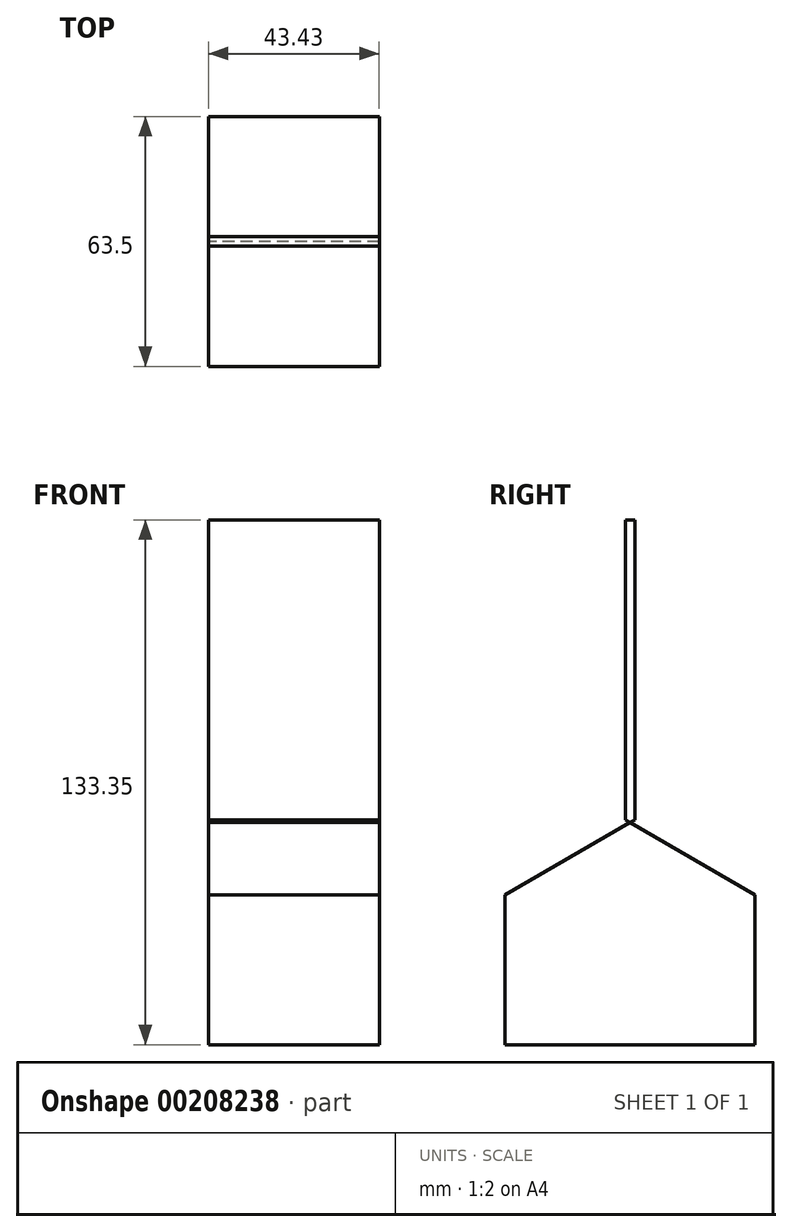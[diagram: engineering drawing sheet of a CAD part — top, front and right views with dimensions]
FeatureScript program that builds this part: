
annotation { "Feature Type Name" : "Feature", "Feature Type Description" : "" }
export const myFeature = defineFeature(function(context is Context, id is Id, definition is map)
    precondition{}
    {
        {
            var Q0;
            Q0=qCreatedBy(makeId("Right.planeOp"),FACE);
            var sketch = newSketch(context, id + "F0", { "sketchPlane" : qUnion([Q0])});
            skLineSegment(sketch, "E0.bottom", {"start": v(-31.75, -65.47) * mm, "end": v(31.75, -65.47) * mm});
            skLineSegment(sketch, "E0.left", {"start": v(-31.75, -65.47) * mm, "end": v(-31.75, -27.37) * mm});
            skLineSegment(sketch, "E0.right", {"start": v(31.75, -65.47) * mm, "end": v(31.75, -27.37) * mm});
            skPoint(sketch, "E0.middle", {"position": v(0, -46.42) * mm});
            skLineSegment(sketch, "E1", {"start": v(31.75, -27.37) * mm, "end": v(-1.25, -8.32) * mm});
            skLineSegment(sketch, "E2", {"start": v(-1.25, 67.88) * mm, "end": v(-1.25, -8.32) * mm});
            skLineSegment(sketch, "E3", {"start": v(0, 67.88) * mm, "end": v(-1.25, 67.88) * mm});
            skLineSegment(sketch, "E4.MirrorCS", {"start": v(-31.75, -27.37) * mm, "end": v(1.25, -8.32) * mm});
            skLineSegment(sketch, "E5.MirrorCS", {"start": v(1.25, 67.88) * mm, "end": v(1.25, -8.32) * mm});
            skLineSegment(sketch, "E6.MirrorCS", {"start": v(0, 67.88) * mm, "end": v(1.25, 67.88) * mm});
            skSolve(sketch);
        }
        {
            var Q0;
            Q0 = qSketchRegion(id + "F0", true);
            extrude(context, id + "F1", {"entities" : qUnion([Q0]), "depth" : 43.43 * mm});
        }
    });
